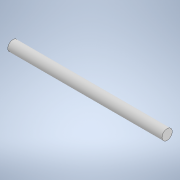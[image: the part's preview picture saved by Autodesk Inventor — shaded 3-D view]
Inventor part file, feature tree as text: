
AUTODESK INVENTOR PART (.ipt)
format: ipt  version: 2020 (Build 240168000, 168)  size: 92,160 bytes
history: native  units: mm
features: other x1, extrude x1, sketch x1
ambient origin geometry x8: Origin, YZ Plane, XZ Plane, XY Plane, X Axis, Y Axis, Z Axis, Center Point
bodies: Body1 (feature_tree)
feature tree (3):
  other  "Твердое тело1"
  extrude  "Выдавливание1"  Depth=4.0mm
  sketch  "Эскиз1"
